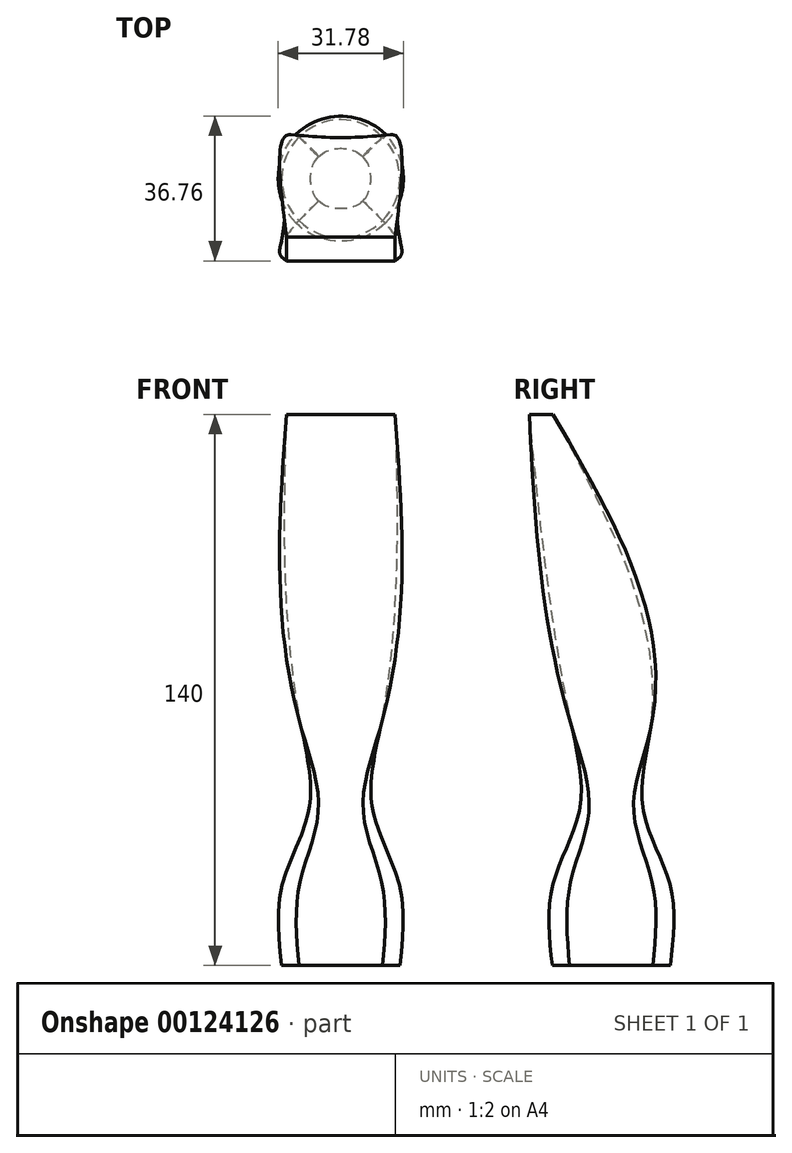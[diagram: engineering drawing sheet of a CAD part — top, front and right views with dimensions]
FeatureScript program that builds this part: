
annotation { "Feature Type Name" : "Feature", "Feature Type Description" : "" }
export const myFeature = defineFeature(function(context is Context, id is Id, definition is map)
    precondition{}
    {
        {
            var Q0;
            Q0=qCreatedBy(makeId("Top.planeOp"),FACE);
            var sketch = newSketch(context, id + "F0", { "sketchPlane" : qUnion([Q0])});
            skCircle(sketch, "E0", {"center": v(0, 0) * mm, "radius": 15 * mm});
            skSolve(sketch);
        }
        {
            var Q0;
            Q0=qCreatedBy(makeId("Top.planeOp"),FACE);
            cPlane(context, id + "F1", {"entities" : qUnion([Q0]), "cplaneType" : CPlaneType.OFFSET, "offset" : 20 * mm, "width" : 150 * mm, "height" : 150 * mm});
        }
        {
            var Q0;
            Q0=qCreatedBy(id+"F1.planeOp",FACE);
            var sketch = newSketch(context, id + "F2", { "sketchPlane" : qUnion([Q0])});
            skCircle(sketch, "E1", {"center": v(0, 0) * mm, "radius": 15 * mm});
            skSolve(sketch);
        }
        {
            var Q0;
            Q0=qCreatedBy(id+"F1.planeOp",FACE);
            cPlane(context, id + "F3", {"entities" : qUnion([Q0]), "cplaneType" : CPlaneType.OFFSET, "offset" : 20 * mm, "width" : 150 * mm, "height" : 150 * mm});
        }
        {
            var Q0;
            Q0=qCreatedBy(id+"F3.planeOp",FACE);
            var sketch = newSketch(context, id + "F4", { "sketchPlane" : qUnion([Q0])});
            skCircle(sketch, "E2", {"center": v(0, 0) * mm, "radius": 8 * mm});
            skSolve(sketch);
        }
        {
            var Q0;
            Q0=qCreatedBy(id+"F3.planeOp",FACE);
            cPlane(context, id + "F5", {"entities" : qUnion([Q0]), "cplaneType" : CPlaneType.OFFSET, "offset" : 20 * mm, "width" : 150 * mm, "height" : 150 * mm});
        }
        {
            var Q0;
            Q0=qCreatedBy(id+"F5.planeOp",FACE);
            var sketch = newSketch(context, id + "F6", { "sketchPlane" : qUnion([Q0])});
            skLineSegment(sketch, "E3.bottom", {"start": v(9.91, 9.91) * mm, "end": v(-9.91, 9.91) * mm});
            skLineSegment(sketch, "E3.top", {"start": v(9.91, -9.91) * mm, "end": v(-9.91, -9.91) * mm});
            skLineSegment(sketch, "E3.left", {"start": v(9.91, 9.91) * mm, "end": v(9.91, -9.91) * mm});
            skLineSegment(sketch, "E3.right", {"start": v(-9.91, 9.91) * mm, "end": v(-9.91, -9.91) * mm});
            skPoint(sketch, "E3.middle", {"position": v(0, 0) * mm});
            skSolve(sketch);
        }
        {
            var Q0;
            Q0=qCreatedBy(id+"F5.planeOp",FACE);
            cPlane(context, id + "F7", {"entities" : qUnion([Q0]), "cplaneType" : CPlaneType.OFFSET, "offset" : 80 * mm, "width" : 150 * mm, "height" : 150 * mm});
        }
        {
            var Q0;
            Q0=qCreatedBy(id+"F7.planeOp",FACE);
            var sketch = newSketch(context, id + "F8", { "sketchPlane" : qUnion([Q0])});
            skLineSegment(sketch, "E4.bottom", {"start": v(13.78, -20.85) * mm, "end": v(-13.78, -20.85) * mm});
            skLineSegment(sketch, "E4.top", {"start": v(13.78, -14.85) * mm, "end": v(-13.78, -14.85) * mm});
            skLineSegment(sketch, "E4.left", {"start": v(13.78, -20.85) * mm, "end": v(13.78, -14.85) * mm});
            skLineSegment(sketch, "E4.right", {"start": v(-13.78, -20.85) * mm, "end": v(-13.78, -14.85) * mm});
            skPoint(sketch, "E4.middle", {"position": v(0, -17.85) * mm});
            skSolve(sketch);
        }
        {
            var Q0;
            Q0=makeQuery(id+"F0.imprint","IMPRINT",FACE,{"disambiguationData":[TD([[makeQuery(id+"F0.imprint","IMPRINT",EDGE,{"derivedFrom":sQuery(id+"F0.wireOp",EDGE,"E0")}),1.0]])]});
            var Q1;
            Q1=makeQuery(id+"F2.imprint","IMPRINT",FACE,{"disambiguationData":[TD([[makeQuery(id+"F2.imprint","IMPRINT",EDGE,{"derivedFrom":sQuery(id+"F2.wireOp",EDGE,"E1")}),1.0]])]});
            var Q2;
            Q2=makeQuery(id+"F4.imprint","IMPRINT",FACE,{"disambiguationData":[TD([[makeQuery(id+"F4.imprint","IMPRINT",EDGE,{"derivedFrom":sQuery(id+"F4.wireOp",EDGE,"E2")}),1.0]])]});
            var Q3;
            Q3=makeQuery(id+"F6.imprint","IMPRINT",FACE,{"disambiguationData":[TD([[makeQuery(id+"F6.imprint","IMPRINT",EDGE,{"derivedFrom":sQuery(id+"F6.wireOp",EDGE,"E3.bottom")}),1.0]])]});
            var Q4;
            Q4=makeQuery(id+"F8.imprint","IMPRINT",FACE,{"disambiguationData":[TD([[makeQuery(id+"F8.imprint","IMPRINT",EDGE,{"derivedFrom":sQuery(id+"F8.wireOp",EDGE,"E4.bottom")}),-1.0]])]});
            loft(context, id + "F9", {"sheetProfilesArray" : [{ "sheetProfileEntities" : qUnion([Q0]) }, { "sheetProfileEntities" : qUnion([Q1]) }, { "sheetProfileEntities" : qUnion([Q2]) }, { "sheetProfileEntities" : qUnion([Q3]) }, { "sheetProfileEntities" : qUnion([Q4]) }]});
        }
    });
